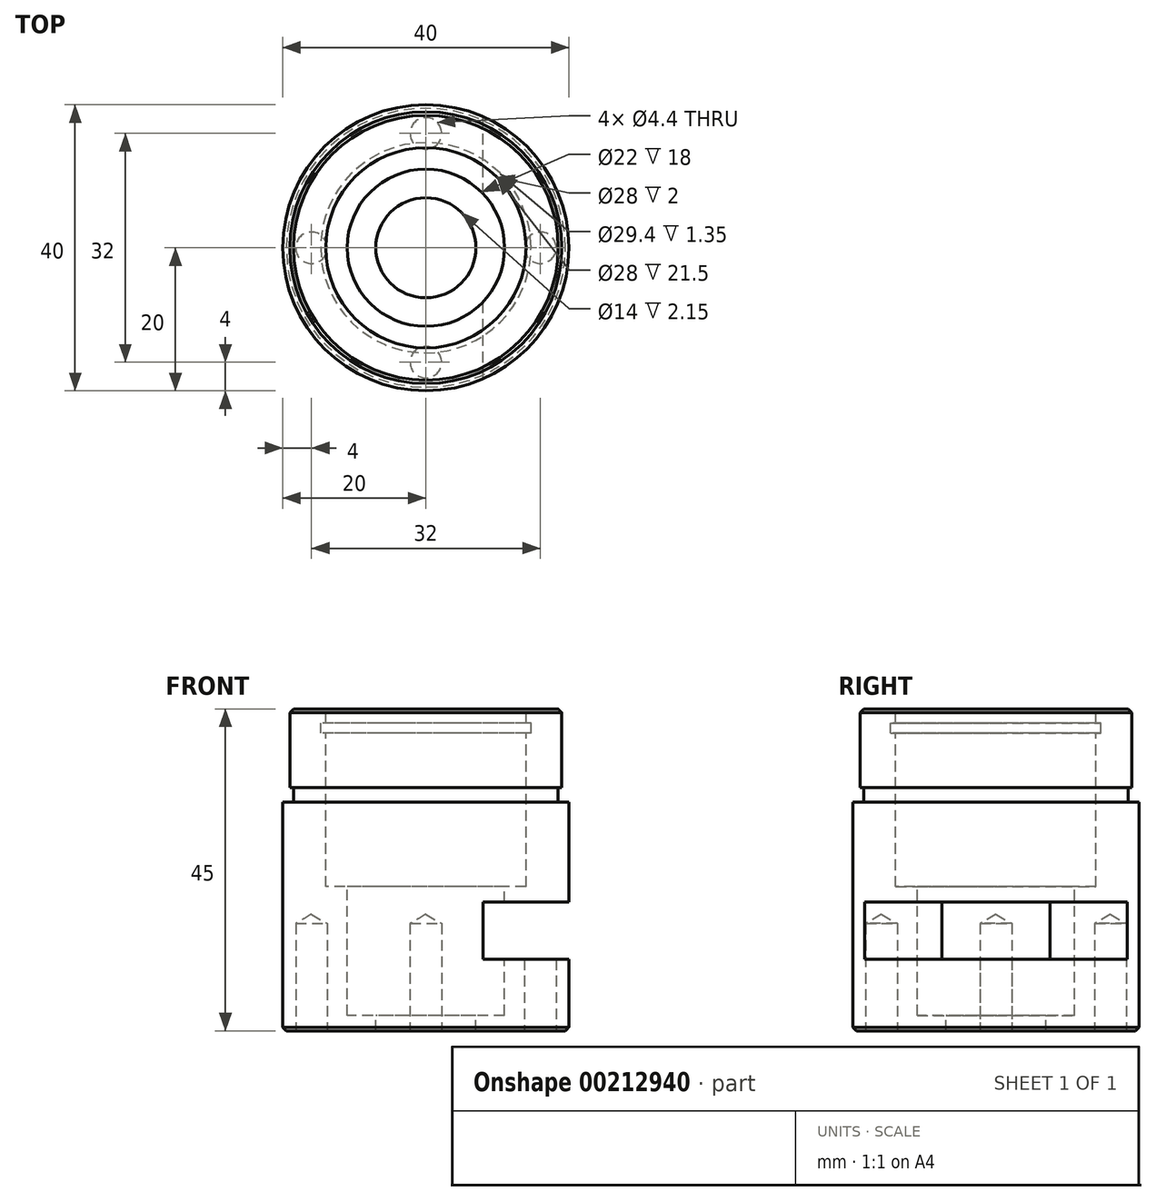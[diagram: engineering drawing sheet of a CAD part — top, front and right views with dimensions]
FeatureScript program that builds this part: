
annotation { "Feature Type Name" : "Feature", "Feature Type Description" : "" }
export const myFeature = defineFeature(function(context is Context, id is Id, definition is map)
    precondition{}
    {
        {
            var Q0;
            Q0=qCreatedBy(makeId("Top.planeOp"),FACE);
            var sketch = newSketch(context, id + "F0", { "sketchPlane" : qUnion([Q0])});
            skCircle(sketch, "E0", {"center": v(0, 0) * mm, "radius": 20 * mm});
            skSolve(sketch);
        }
        {
            var Q0;
            Q0 = qSketchRegion(id + "F0", true);
            extrude(context, id + "F1", {"entities" : qUnion([Q0]), "depth" : 32 * mm});
        }
        {
            var Q0;
            Q0=makeQuery(id+"F1.opExtrude","CAP_FACE",FACE,{"disambiguationData":[OSD([sQuery(id+"F0.wireOp",EDGE,"E0")])],"isStart":false});
            var sketch = newSketch(context, id + "F2", { "sketchPlane" : qUnion([Q0])});
            skCircle(sketch, "E1", {"center": v(0, 0) * mm, "radius": 18.5 * mm});
            skSolve(sketch);
        }
        {
            var Q0;
            Q0 = qSketchRegion(id + "F2", true);
            extrude(context, id + "F3", {"entities" : qUnion([Q0]), "operationType" : NewBodyOperationType.ADD, "depth" : 2 * mm});
        }
        {
            var Q0;
            Q0=makeQuery(id+"F3.opExtrude","CAP_FACE",FACE,{"disambiguationData":[OSD([sQuery(id+"F2.wireOp",EDGE,"E1")])],"isStart":false});
            var sketch = newSketch(context, id + "F4", { "sketchPlane" : qUnion([Q0])});
            skCircle(sketch, "E2", {"center": v(0, 0) * mm, "radius": 19 * mm});
            skSolve(sketch);
        }
        {
            var Q0;
            Q0 = qSketchRegion(id + "F4", true);
            extrude(context, id + "F5", {"entities" : qUnion([Q0]), "operationType" : NewBodyOperationType.ADD, "depth" : 11 * mm});
        }
        {
            var Q0;
            Q0=makeQuery(id+"F5.opExtrude","CAP_FACE",FACE,{"disambiguationData":[OSD([sQuery(id+"F4.wireOp",EDGE,"E2")])],"isStart":false});
            var sketch = newSketch(context, id + "F6", { "sketchPlane" : qUnion([Q0])});
            skCircle(sketch, "E3", {"center": v(0, 0) * mm, "radius": 14 * mm});
            skSolve(sketch);
        }
        {
            var Q0;
            Q0 = qSketchRegion(id + "F6", true);
            extrude(context, id + "F7", {"entities" : qUnion([Q0]), "operationType" : NewBodyOperationType.REMOVE, "oppositeDirection" : true, "depth" : 2 * mm});
        }
        {
            var Q0;
            Q0=makeQuery(id+"F7.boolean.opBoolean","COPY",FACE,{"derivedFrom":makeQuery(id+"F7.opExtrude","CAP_FACE",FACE,{"disambiguationData":[OSD([sQuery(id+"F6.wireOp",EDGE,"E3")])],"isStart":false})});
            var sketch = newSketch(context, id + "F8", { "sketchPlane" : qUnion([Q0])});
            skCircle(sketch, "E4", {"center": v(0, 0) * mm, "radius": 14.7 * mm});
            skSolve(sketch);
        }
        {
            var Q0;
            Q0 = qSketchRegion(id + "F8", true);
            extrude(context, id + "F9", {"entities" : qUnion([Q0]), "operationType" : NewBodyOperationType.REMOVE, "oppositeDirection" : true, "depth" : 1.35 * mm});
        }
        {
            var Q0;
            Q0=makeQuery(id+"F9.boolean.opBoolean","COPY",FACE,{"derivedFrom":makeQuery(id+"F9.opExtrude","CAP_FACE",FACE,{"disambiguationData":[OSD([sQuery(id+"F8.wireOp",EDGE,"E4")])],"isStart":false})});
            var sketch = newSketch(context, id + "F10", { "sketchPlane" : qUnion([Q0])});
            skCircle(sketch, "E5", {"center": v(0, 0) * mm, "radius": 14 * mm});
            skSolve(sketch);
        }
        {
            var Q0;
            Q0 = qSketchRegion(id + "F10", true);
            extrude(context, id + "F11", {"entities" : qUnion([Q0]), "operationType" : NewBodyOperationType.REMOVE, "oppositeDirection" : true, "depth" : (25 - (1.5 + 2)) * mm});
        }
        {
            var Q0;
            Q0=makeQuery(id+"F11.boolean.opBoolean","COPY",FACE,{"derivedFrom":makeQuery(id+"F11.opExtrude","CAP_FACE",FACE,{"disambiguationData":[OSD([sQuery(id+"F10.wireOp",EDGE,"E5")])],"isStart":false})});
            var sketch = newSketch(context, id + "F12", { "sketchPlane" : qUnion([Q0])});
            skCircle(sketch, "E6", {"center": v(0, 0) * mm, "radius": 11 * mm});
            skSolve(sketch);
        }
        {
            var Q0;
            Q0 = qSketchRegion(id + "F12", true);
            extrude(context, id + "F13", {"entities" : qUnion([Q0]), "operationType" : NewBodyOperationType.REMOVE, "oppositeDirection" : true, "depth" : 18 * mm});
        }
        {
            var Q0;
            Q0=makeQuery(id+"F13.boolean.opBoolean","COPY",FACE,{"derivedFrom":makeQuery(id+"F13.opExtrude","CAP_FACE",FACE,{"disambiguationData":[OSD([sQuery(id+"F12.wireOp",EDGE,"E6")])],"isStart":false})});
            var sketch = newSketch(context, id + "F14", { "sketchPlane" : qUnion([Q0])});
            skCircle(sketch, "E7", {"center": v(0, 0) * mm, "radius": 7 * mm});
            skSolve(sketch);
        }
        {
            var Q0;
            Q0 = qSketchRegion(id + "F14", true);
            extrude(context, id + "F15", {"entities" : qUnion([Q0]), "operationType" : NewBodyOperationType.REMOVE, "oppositeDirection" : true, "depth" : 25 * mm});
        }
        {
            var Q0;
            Q0=makeQuery(id+"F1.opExtrude","CAP_FACE",FACE,{"disambiguationData":[OSD([sQuery(id+"F0.wireOp",EDGE,"E0")])],"isStart":true});
            var sketch = newSketch(context, id + "F16", { "sketchPlane" : qUnion([Q0])});
            skPoint(sketch, "E8", {"position": v(-16, 0) * mm});
            skPoint(sketch, "E9", {"position": v(16, 0) * mm});
            skPoint(sketch, "E10", {"position": v(0, 0) * mm});
            skPoint(sketch, "E11", {"position": v(-0.17, -0.12) * mm});
            skPoint(sketch, "E12", {"position": v(0, 16) * mm});
            skPoint(sketch, "E13", {"position": v(0, -16) * mm});
            skSolve(sketch);
        }
        {
            var Q0;
            Q0=sQuery(id+"F16.wireOp",VERTEX,"E8");
            var Q1;
            Q1=sQuery(id+"F16.wireOp",VERTEX,"E12");
            var Q2;
            Q2=sQuery(id+"F16.wireOp",VERTEX,"E9");
            var Q3;
            Q3=sQuery(id+"F16.wireOp",VERTEX,"E13");
            var Q4;
            Q4=makeQuery(id+"F1.opExtrude","SWEPT_BODY",BODY,{"disambiguationData":[OSD([sQuery(id+"F0.wireOp",EDGE,"E0")])]});
            hole(context, id + "F17", {"style" : HoleStyle.SIMPLE, "endStyle" : HoleEndStyle.BLIND, "standardTappedOrClearance" : lookupTablePath({ "standard" : "ISO", "fit" : "Normal", "size" : "M4", "type" : "Clearance" }), "standardBlindInLast" : lookupTablePath({ "fit" : "Standard", "standard" : "ISO", "size" : "M4", "type" : "Clearance" }), "holeDiameter" : 4.4 * mm, "holeDepth" : 15 * mm, "locations" : qUnion([Q0, Q1, Q2, Q3]), "scope" : qUnion([Q4])});
        }
        {
            var Q0;
            Q0=makeQuery(id+"F1.opExtrude","CAP_FACE",FACE,{"disambiguationData":[OSD([sQuery(id+"F0.wireOp",EDGE,"E0")])],"isStart":true});
            var sketch = newSketch(context, id + "F18", { "sketchPlane" : qUnion([Q0])});
            skLineSegment(sketch, "E14.bottom", {"start": v(8, 21.56) * mm, "end": v(28, 21.56) * mm});
            skLineSegment(sketch, "E14.top", {"start": v(8, -22.11) * mm, "end": v(28, -22.11) * mm});
            skLineSegment(sketch, "E14.left", {"start": v(8, 21.56) * mm, "end": v(8, -22.11) * mm});
            skLineSegment(sketch, "E14.right", {"start": v(28, 21.56) * mm, "end": v(28, -22.11) * mm});
            skSolve(sketch);
        }
        {
            var Q0;
            Q0 = qSketchRegion(id + "F18", true);
            extrude(context, id + "F19", {"entities" : qUnion([Q0]), "operationType" : NewBodyOperationType.REMOVE, "oppositeDirection" : true, "depth" : 18 * mm, "hasSecondDirection" : true, "secondDirectionOppositeDirection" : true, "secondDirectionDepth" : 10 * mm});
        }
        {
            var Q0;
            Q0=makeQuery(id+"F1.opExtrude","CAP_EDGE",EDGE,{"disambiguationData":[OSD([sQuery(id+"F0.wireOp",EDGE,"E0")])],"isStart":true});
            var Q1;
            Q1=makeQuery(id+"F5.opExtrude","CAP_EDGE",EDGE,{"disambiguationData":[OSD([sQuery(id+"F4.wireOp",EDGE,"E2")])],"isStart":false});
            chamfer(context, id + "F20", {"entities" : qUnion([Q0, Q1]), "width" : .5 * mm, "tangentPropagation" : true});
        }
    });
